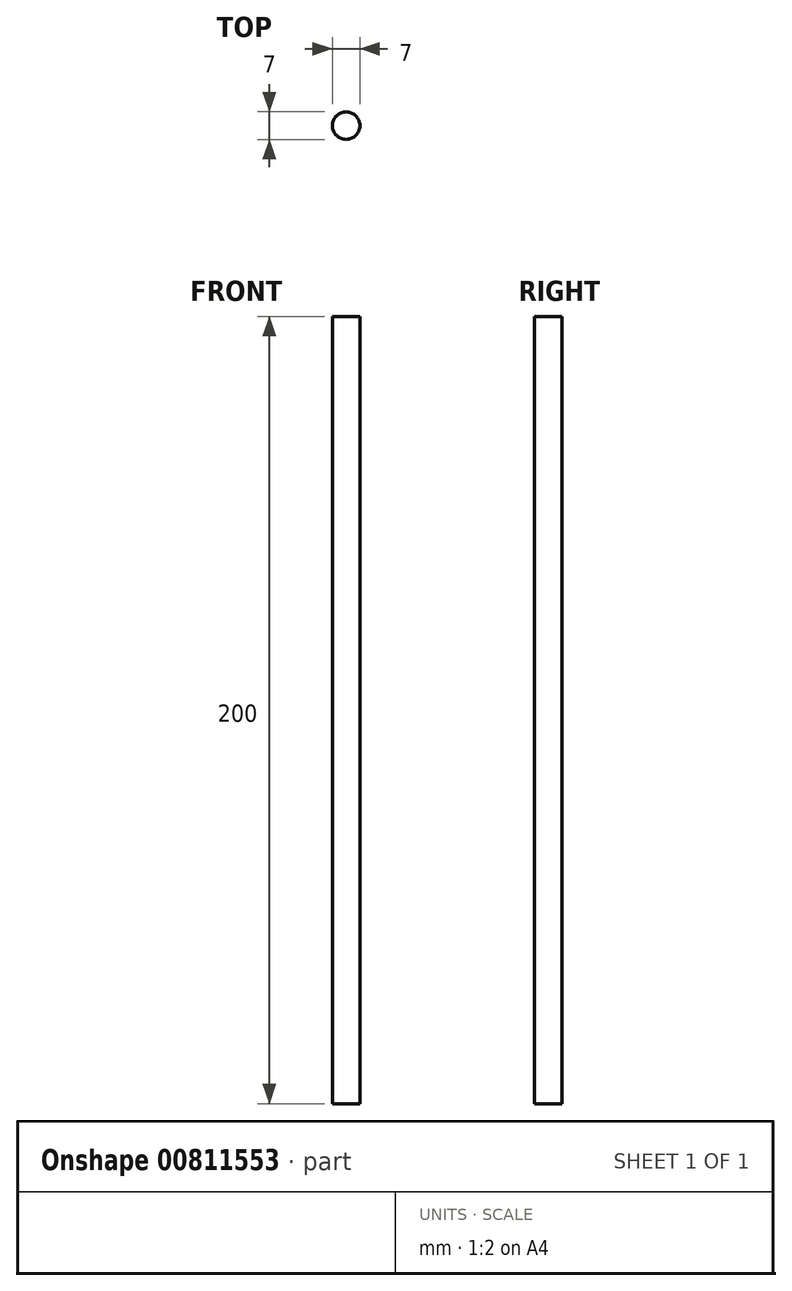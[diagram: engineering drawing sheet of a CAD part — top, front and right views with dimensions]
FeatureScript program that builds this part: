
annotation { "Feature Type Name" : "Feature", "Feature Type Description" : "" }
export const myFeature = defineFeature(function(context is Context, id is Id, definition is map)
    precondition{}
    {
        {
            var Q0;
            Q0=qCreatedBy(makeId("Top.planeOp"),FACE);
            var sketch = newSketch(context, id + "F0", { "sketchPlane" : qUnion([Q0])});
            skCircle(sketch, "E0", {"center": v(0, 0) * mm, "radius": 3.5 * mm});
            skSolve(sketch);
        }
        {
            var Q0;
            Q0 = qSketchRegion(id + "F0", true);
            extrude(context, id + "F1", {"entities" : qUnion([Q0]), "depth" : 200 * mm, "offsetDistance" : 25 * mm});
        }
        {
            var Q0;
            Q0=makeQuery(id+"F1.opExtrude","CAP_FACE",FACE,{"disambiguationData":[OSD([sQuery(id+"F0.wireOp",EDGE,"E0")])],"isStart":false});
            var sketch = newSketch(context, id + "F2", { "sketchPlane" : qUnion([Q0])});
            skLineSegment(sketch, "E1", {"start": v(0, 3.5) * mm, "end": v(0, -3.5) * mm, "construction": true});
            skLineSegment(sketch, "E2", {"start": v(3.5, 0) * mm, "end": v(3.5, -8.99) * mm, "construction": true});
            skSolve(sketch);
        }
        {
            var Q0;
            Q0=sQuery(id+"F2.wireOp",EDGE,"E2");
            cPlane(context, id + "F3", {"entities" : qUnion([Q0]), "cplaneType" : CPlaneType.LINE_ANGLE, "offset" : 25 * mm, "angle" : 45 * degree, "width" : 150 * mm, "height" : 150 * mm});
        }
        {
            var Q0;
            Q0=qCreatedBy(id+"F3.planeOp",FACE);
            var sketch = newSketch(context, id + "F4", { "sketchPlane" : qUnion([Q0])});
            skLineSegment(sketch, "E3.bottom", {"start": v(131.74, -6.97) * mm, "end": v(155.76, -6.97) * mm});
            skLineSegment(sketch, "E3.top", {"start": v(131.74, 6.97) * mm, "end": v(155.76, 6.97) * mm});
            skLineSegment(sketch, "E3.left", {"start": v(131.74, -6.97) * mm, "end": v(131.74, 6.97) * mm});
            skLineSegment(sketch, "E3.right", {"start": v(155.76, -6.97) * mm, "end": v(155.76, 6.97) * mm});
            skPoint(sketch, "E3.middle", {"position": v(143.75, 0) * mm});
            skSolve(sketch);
        }
        {
            var Q0;
            Q0=makeQuery(id+"F2.imprint","IMPRINT",FACE,{"disambiguationData":[TD([[makeQuery(id+"F2.imprint","IMPRINT",EDGE,{"derivedFrom":makeQuery(id+"F1.opExtrude","CAP_EDGE",EDGE,{"disambiguationData":[OSD([sQuery(id+"F0.wireOp",EDGE,"E0")])],"isStart":false})}),1.0]])]});
            var Q1;
            Q1=makeQuery(id+"F4.imprint","IMPRINT",FACE,{"disambiguationData":[TD([[makeQuery(id+"F4.imprint","IMPRINT",EDGE,{"derivedFrom":sQuery(id+"F4.wireOp",EDGE,"E3.bottom")}),1.0]])]});
            extrude(context, id + "F5", {"entities" : qUnion([Q0, Q1]), "operationType" : NewBodyOperationType.REMOVE, "depth" : 25 * mm, "offsetDistance" : 25 * mm});
        }
    });
